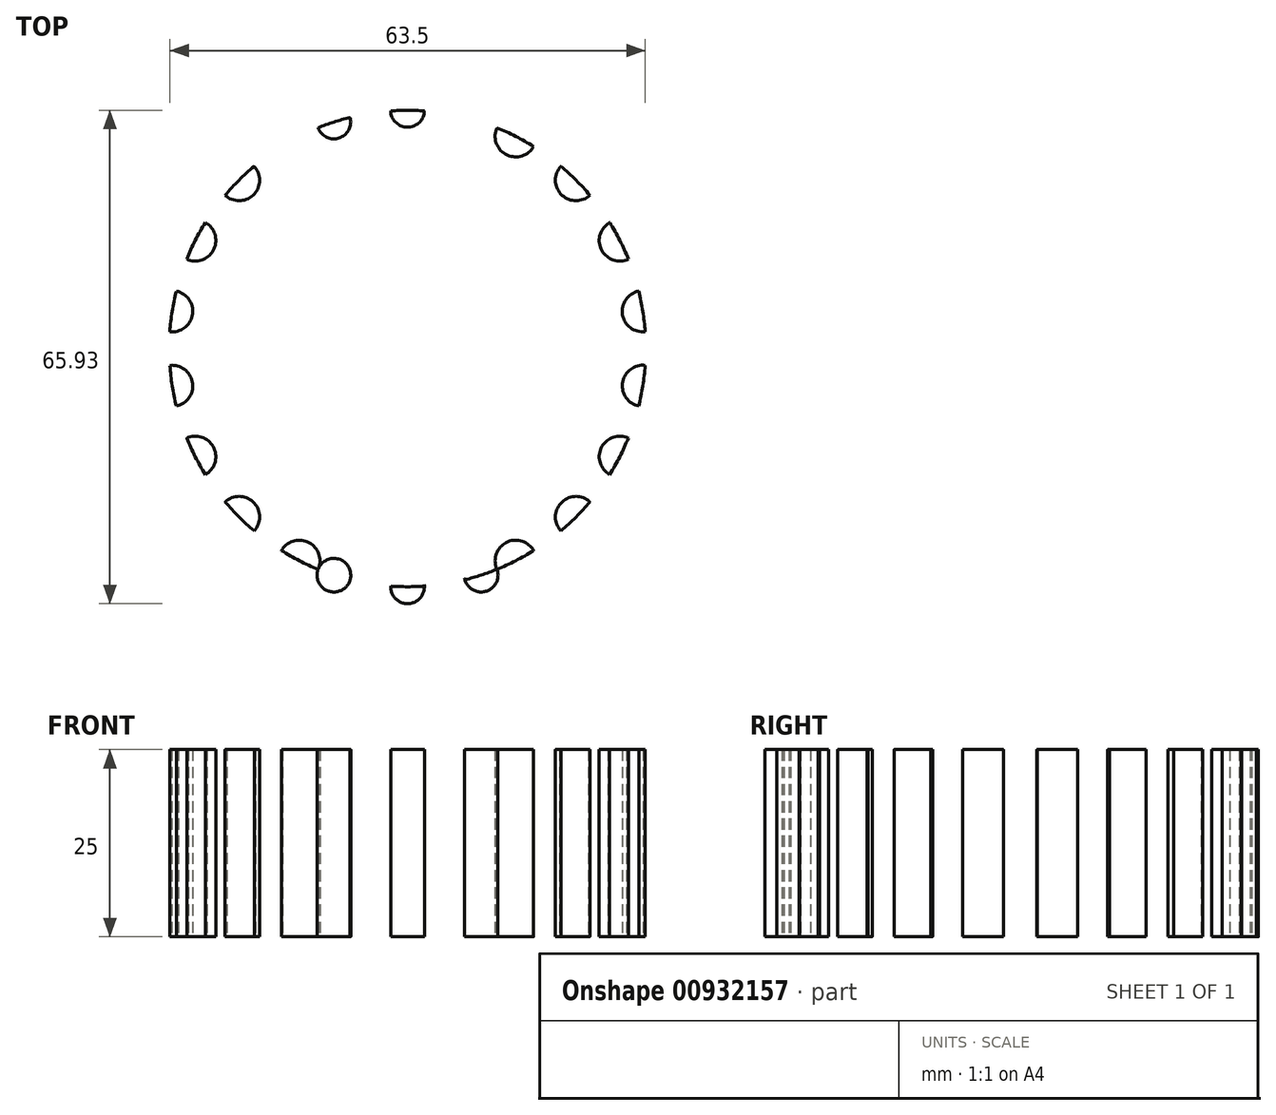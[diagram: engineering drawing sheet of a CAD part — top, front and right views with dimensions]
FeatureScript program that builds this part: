
annotation { "Feature Type Name" : "Feature", "Feature Type Description" : "" }
export const myFeature = defineFeature(function(context is Context, id is Id, definition is map)
    precondition{}
    {
        {
            var Q0;
            Q0=qCreatedBy(makeId("Top.planeOp"),FACE);
            var sketch = newSketch(context, id + "F0", { "sketchPlane" : qUnion([Q0])});
            skCircle(sketch, "E0", {"center": v(0, 0) * mm, "radius": 31.83 * mm});
            skCircle(sketch, "E1", {"center": v(0, 31.83) * mm, "radius": 2.25 * mm});
            skCircle(sketch, "E2.1.0", {"center": v(-9.84, 30.27) * mm, "radius": 2.25 * mm});
            skCircle(sketch, "E2.2.0", {"center": v(-18.71, 25.75) * mm, "radius": 2.25 * mm});
            skCircle(sketch, "E2.3.0", {"center": v(-25.76, 18.7) * mm, "radius": 2.25 * mm});
            skCircle(sketch, "E2.4.0", {"center": v(-30.28, 9.83) * mm, "radius": 2.25 * mm});
            skCircle(sketch, "E2.5.0", {"center": v(-31.84, 0) * mm, "radius": 2.25 * mm});
            skCircle(sketch, "E2.6.0", {"center": v(-30.28, -9.85) * mm, "radius": 2.25 * mm});
            skCircle(sketch, "E2.7.0", {"center": v(-25.76, -18.72) * mm, "radius": 2.25 * mm});
            skCircle(sketch, "E2.8.0", {"center": v(-18.71, -25.77) * mm, "radius": 2.25 * mm});
            skCircle(sketch, "E2.9.0", {"center": v(-9.84, -30.29) * mm, "radius": 2.25 * mm});
            skCircle(sketch, "E2.10.0", {"center": v(0, -31.85) * mm, "radius": 2.25 * mm});
            skCircle(sketch, "E2.11.0", {"center": v(9.84, -30.29) * mm, "radius": 2.25 * mm});
            skCircle(sketch, "E2.12.0", {"center": v(18.72, -25.77) * mm, "radius": 2.25 * mm});
            skCircle(sketch, "E2.13.0", {"center": v(25.76, -18.72) * mm, "radius": 2.25 * mm});
            skCircle(sketch, "E2.14.0", {"center": v(30.28, -9.85) * mm, "radius": 2.25 * mm});
            skCircle(sketch, "E2.15.0", {"center": v(31.84, 0) * mm, "radius": 2.25 * mm});
            skCircle(sketch, "E2.16.0", {"center": v(30.28, 9.83) * mm, "radius": 2.25 * mm});
            skCircle(sketch, "E2.17.0", {"center": v(25.76, 18.7) * mm, "radius": 2.25 * mm});
            skCircle(sketch, "E2.18.0", {"center": v(18.71, 25.75) * mm, "radius": 2.25 * mm});
            skCircle(sketch, "E2.19.0", {"center": v(9.84, 30.27) * mm, "radius": 2.25 * mm});
            skArc(sketch, "E3", {"start": v(-2.25, 31.75) * mm, "mid": v(-4.55, 28.72) * mm, "end": v(-7.68, 30.9) * mm});
            skArc(sketch, "E4.1.0", {"start": v(-11.95, 29.5) * mm, "mid": v(-13.2, 25.91) * mm, "end": v(-16.85, 27) * mm});
            skArc(sketch, "E4.2.0", {"start": v(-20.48, 24.37) * mm, "mid": v(-20.56, 20.56) * mm, "end": v(-24.37, 20.48) * mm});
            skArc(sketch, "E4.3.0", {"start": v(-27, 16.84) * mm, "mid": v(-25.91, 13.2) * mm, "end": v(-29.5, 11.95) * mm});
            skArc(sketch, "E4.4.0", {"start": v(-30.9, 7.67) * mm, "mid": v(-28.72, 4.55) * mm, "end": v(-31.75, 2.25) * mm});
            skArc(sketch, "E4.5.0", {"start": v(-31.75, -2.25) * mm, "mid": v(-28.72, -4.55) * mm, "end": v(-30.9, -7.68) * mm});
            skArc(sketch, "E4.6.0", {"start": v(-29.5, -11.95) * mm, "mid": v(-25.91, -13.2) * mm, "end": v(-27, -16.85) * mm});
            skArc(sketch, "E4.7.0", {"start": v(-24.37, -20.48) * mm, "mid": v(-20.56, -20.56) * mm, "end": v(-20.48, -24.37) * mm});
            skArc(sketch, "E4.8.0", {"start": v(-16.84, -27) * mm, "mid": v(-13.2, -25.91) * mm, "end": v(-11.95, -29.5) * mm});
            skArc(sketch, "E4.9.0", {"start": v(-7.67, -30.9) * mm, "mid": v(-4.55, -28.72) * mm, "end": v(-2.25, -31.75) * mm});
            skArc(sketch, "E4.10.0", {"start": v(2.25, -31.75) * mm, "mid": v(4.55, -28.72) * mm, "end": v(7.68, -30.9) * mm});
            skArc(sketch, "E4.11.0", {"start": v(11.95, -29.5) * mm, "mid": v(13.2, -25.91) * mm, "end": v(16.85, -27) * mm});
            skArc(sketch, "E4.12.0", {"start": v(20.48, -24.37) * mm, "mid": v(20.56, -20.56) * mm, "end": v(24.37, -20.48) * mm});
            skArc(sketch, "E4.13.0", {"start": v(27, -16.84) * mm, "mid": v(25.91, -13.2) * mm, "end": v(29.5, -11.95) * mm});
            skArc(sketch, "E4.14.0", {"start": v(30.9, -7.67) * mm, "mid": v(28.72, -4.55) * mm, "end": v(31.75, -2.25) * mm});
            skArc(sketch, "E4.15.0", {"start": v(31.75, 2.25) * mm, "mid": v(28.72, 4.55) * mm, "end": v(30.9, 7.68) * mm});
            skArc(sketch, "E4.16.0", {"start": v(29.5, 11.95) * mm, "mid": v(25.91, 13.2) * mm, "end": v(27, 16.85) * mm});
            skArc(sketch, "E4.17.0", {"start": v(24.37, 20.48) * mm, "mid": v(20.56, 20.56) * mm, "end": v(20.48, 24.37) * mm});
            skArc(sketch, "E4.18.0", {"start": v(16.84, 27) * mm, "mid": v(13.2, 25.91) * mm, "end": v(11.95, 29.5) * mm});
            skArc(sketch, "E4.19.0", {"start": v(7.67, 30.9) * mm, "mid": v(4.55, 28.72) * mm, "end": v(2.25, 31.75) * mm});
            skSolve(sketch);
        }
        {
            var Q0;
            {var subQ1=sQuery(id+"F0.wireOp",EDGE,"E0");var subQ20=sQuery(id+"F0.wireOp",EDGE,"E4.15.0");var subQ76=makeQuery(id+"F0.imprint","INTERSECT",VERTEX,{"disambiguationData":[OD(0.0)],"derivedFrom":[subQ1,subQ20]});Q0=makeQuery(id+"F0.imprint","IMPRINT",FACE,{"disambiguationData":[TD([[makeQuery(id+"F0.imprint","IMPRINT",EDGE,{"disambiguationData":[TD([[subQ76,1.0]])],"derivedFrom":subQ1}),1.0]])]});}
            var Q1;
            {var subQ0=sQuery(id+"F0.wireOp",EDGE,"E0");var subQ1=makeQuery(id+"F0.imprint","INTERSECT",VERTEX,{"disambiguationData":[OD(0.0)],"derivedFrom":[subQ0,sQuery(id+"F0.wireOp",EDGE,"E4.2.0")]});Q1=makeQuery(id+"F0.imprint","IMPRINT",FACE,{"disambiguationData":[TD([[makeQuery(id+"F0.imprint","IMPRINT",EDGE,{"disambiguationData":[TD([[subQ1,1.0]])],"derivedFrom":subQ0}),-1.0]])]});}
            var Q2;
            {var subQ4=sQuery(id+"F0.wireOp",EDGE,"E0");var subQ6=sQuery(id+"F0.wireOp",EDGE,"E4.2.0");var subQ8=makeQuery(id+"F0.imprint","INTERSECT",VERTEX,{"disambiguationData":[OD(0.0)],"derivedFrom":[subQ4,subQ6]});Q2=makeQuery(id+"F0.imprint","IMPRINT",FACE,{"disambiguationData":[TD([[makeQuery(id+"F0.imprint","IMPRINT",EDGE,{"disambiguationData":[TD([[subQ8,1.0]])],"derivedFrom":subQ4}),1.0]])]});}
            var Q3;
            {var subQ1=sQuery(id+"F0.wireOp",EDGE,"E0");var subQ3=makeQuery(id+"F0.imprint","INTERSECT",VERTEX,{"disambiguationData":[OD(0.0)],"derivedFrom":[subQ1,sQuery(id+"F0.wireOp",EDGE,"E4.1.0")]});Q3=makeQuery(id+"F0.imprint","IMPRINT",FACE,{"disambiguationData":[TD([[makeQuery(id+"F0.imprint","IMPRINT",EDGE,{"disambiguationData":[TD([[subQ3,-1.0]])],"derivedFrom":subQ1}),-1.0]])]});}
            var Q4;
            {var subQ1=sQuery(id+"F0.wireOp",EDGE,"E2.1.0");var subQ4=sQuery(id+"F0.wireOp",EDGE,"E4.1.0");var subQ7=makeQuery(id+"F0.imprint","INTERSECT",VERTEX,{"derivedFrom":[subQ1,subQ4]});Q4=makeQuery(id+"F0.imprint","IMPRINT",FACE,{"disambiguationData":[TD([[makeQuery(id+"F0.imprint","IMPRINT",EDGE,{"disambiguationData":[TD([[subQ7,-1.0]])],"derivedFrom":subQ1}),1.0]])]});}
            var Q5;
            {var subQ0=sQuery(id+"F0.wireOp",EDGE,"E0");var subQ1=makeQuery(id+"F0.imprint","INTERSECT",VERTEX,{"disambiguationData":[OD(1.0)],"derivedFrom":[subQ0,sQuery(id+"F0.wireOp",EDGE,"E4.19.0")]});Q5=makeQuery(id+"F0.imprint","IMPRINT",FACE,{"disambiguationData":[TD([[makeQuery(id+"F0.imprint","IMPRINT",EDGE,{"disambiguationData":[TD([[subQ1,1.0]])],"derivedFrom":subQ0}),-1.0]])]});}
            var Q6;
            {var subQ0=sQuery(id+"F0.wireOp",EDGE,"E3");var subQ1=sQuery(id+"F0.wireOp",EDGE,"E1");var subQ6=makeQuery(id+"F0.imprint","INTERSECT",VERTEX,{"derivedFrom":[subQ1,subQ0]});Q6=makeQuery(id+"F0.imprint","IMPRINT",FACE,{"disambiguationData":[TD([[makeQuery(id+"F0.imprint","IMPRINT",EDGE,{"disambiguationData":[TD([[subQ6,-1.0]])],"derivedFrom":subQ1}),1.0]])]});}
            var Q7;
            {var subQ0=sQuery(id+"F0.wireOp",EDGE,"E0");var subQ1=makeQuery(id+"F0.imprint","INTERSECT",VERTEX,{"disambiguationData":[OD(1.0)],"derivedFrom":[subQ0,sQuery(id+"F0.wireOp",EDGE,"E4.18.0")]});Q7=makeQuery(id+"F0.imprint","IMPRINT",FACE,{"disambiguationData":[TD([[makeQuery(id+"F0.imprint","IMPRINT",EDGE,{"disambiguationData":[TD([[subQ1,1.0]])],"derivedFrom":subQ0}),-1.0]])]});}
            var Q8;
            {var subQ3=sQuery(id+"F0.wireOp",EDGE,"E4.18.0");var subQ5=sQuery(id+"F0.wireOp",EDGE,"E0");var subQ8=makeQuery(id+"F0.imprint","INTERSECT",VERTEX,{"disambiguationData":[OD(1.0)],"derivedFrom":[subQ5,subQ3]});Q8=makeQuery(id+"F0.imprint","IMPRINT",FACE,{"disambiguationData":[TD([[makeQuery(id+"F0.imprint","IMPRINT",EDGE,{"disambiguationData":[TD([[subQ8,-1.0]])],"derivedFrom":subQ5}),1.0]])]});}
            var Q9;
            {var subQ0=sQuery(id+"F0.wireOp",EDGE,"E0");var subQ1=makeQuery(id+"F0.imprint","INTERSECT",VERTEX,{"disambiguationData":[OD(1.0)],"derivedFrom":[subQ0,sQuery(id+"F0.wireOp",EDGE,"E4.17.0")]});Q9=makeQuery(id+"F0.imprint","IMPRINT",FACE,{"disambiguationData":[TD([[makeQuery(id+"F0.imprint","IMPRINT",EDGE,{"disambiguationData":[TD([[subQ1,1.0]])],"derivedFrom":subQ0}),-1.0]])]});}
            var Q10;
            {var subQ0=sQuery(id+"F0.wireOp",EDGE,"E4.17.0");var subQ1=sQuery(id+"F0.wireOp",EDGE,"E0");var subQ2=makeQuery(id+"F0.imprint","INTERSECT",VERTEX,{"disambiguationData":[OD(1.0)],"derivedFrom":[subQ1,subQ0]});Q10=makeQuery(id+"F0.imprint","IMPRINT",FACE,{"disambiguationData":[TD([[makeQuery(id+"F0.imprint","IMPRINT",EDGE,{"disambiguationData":[TD([[subQ2,-1.0]])],"derivedFrom":subQ1}),1.0]])]});}
            var Q11;
            {var subQ0=sQuery(id+"F0.wireOp",EDGE,"E4.16.0");var subQ1=sQuery(id+"F0.wireOp",EDGE,"E0");var subQ2=makeQuery(id+"F0.imprint","INTERSECT",VERTEX,{"disambiguationData":[OD(1.0)],"derivedFrom":[subQ1,subQ0]});Q11=makeQuery(id+"F0.imprint","IMPRINT",FACE,{"disambiguationData":[TD([[makeQuery(id+"F0.imprint","IMPRINT",EDGE,{"disambiguationData":[TD([[subQ2,-1.0]])],"derivedFrom":subQ1}),1.0]])]});}
            var Q12;
            {var subQ0=sQuery(id+"F0.wireOp",EDGE,"E0");var subQ1=makeQuery(id+"F0.imprint","INTERSECT",VERTEX,{"disambiguationData":[OD(1.0)],"derivedFrom":[subQ0,sQuery(id+"F0.wireOp",EDGE,"E4.16.0")]});Q12=makeQuery(id+"F0.imprint","IMPRINT",FACE,{"disambiguationData":[TD([[makeQuery(id+"F0.imprint","IMPRINT",EDGE,{"disambiguationData":[TD([[subQ1,1.0]])],"derivedFrom":subQ0}),-1.0]])]});}
            var Q13;
            {var subQ0=sQuery(id+"F0.wireOp",EDGE,"E4.15.0");var subQ1=sQuery(id+"F0.wireOp",EDGE,"E0");var subQ2=makeQuery(id+"F0.imprint","INTERSECT",VERTEX,{"disambiguationData":[OD(1.0)],"derivedFrom":[subQ1,subQ0]});Q13=makeQuery(id+"F0.imprint","IMPRINT",FACE,{"disambiguationData":[TD([[makeQuery(id+"F0.imprint","IMPRINT",EDGE,{"disambiguationData":[TD([[subQ2,-1.0]])],"derivedFrom":subQ1}),1.0]])]});}
            var Q14;
            {var subQ0=sQuery(id+"F0.wireOp",EDGE,"E4.14.0");var subQ1=sQuery(id+"F0.wireOp",EDGE,"E0");var subQ2=makeQuery(id+"F0.imprint","INTERSECT",VERTEX,{"disambiguationData":[OD(1.0)],"derivedFrom":[subQ1,subQ0]});Q14=makeQuery(id+"F0.imprint","IMPRINT",FACE,{"disambiguationData":[TD([[makeQuery(id+"F0.imprint","IMPRINT",EDGE,{"disambiguationData":[TD([[subQ2,-1.0]])],"derivedFrom":subQ1}),1.0]])]});}
            var Q15;
            {var subQ0=sQuery(id+"F0.wireOp",EDGE,"E0");var subQ1=makeQuery(id+"F0.imprint","INTERSECT",VERTEX,{"disambiguationData":[OD(1.0)],"derivedFrom":[subQ0,sQuery(id+"F0.wireOp",EDGE,"E4.14.0")]});Q15=makeQuery(id+"F0.imprint","IMPRINT",FACE,{"disambiguationData":[TD([[makeQuery(id+"F0.imprint","IMPRINT",EDGE,{"disambiguationData":[TD([[subQ1,1.0]])],"derivedFrom":subQ0}),-1.0]])]});}
            var Q16;
            {var subQ0=sQuery(id+"F0.wireOp",EDGE,"E4.13.0");var subQ1=sQuery(id+"F0.wireOp",EDGE,"E0");var subQ2=makeQuery(id+"F0.imprint","INTERSECT",VERTEX,{"disambiguationData":[OD(1.0)],"derivedFrom":[subQ1,subQ0]});Q16=makeQuery(id+"F0.imprint","IMPRINT",FACE,{"disambiguationData":[TD([[makeQuery(id+"F0.imprint","IMPRINT",EDGE,{"disambiguationData":[TD([[subQ2,-1.0]])],"derivedFrom":subQ1}),1.0]])]});}
            var Q17;
            {var subQ0=sQuery(id+"F0.wireOp",EDGE,"E4.12.0");var subQ1=sQuery(id+"F0.wireOp",EDGE,"E0");var subQ2=makeQuery(id+"F0.imprint","INTERSECT",VERTEX,{"disambiguationData":[OD(1.0)],"derivedFrom":[subQ1,subQ0]});Q17=makeQuery(id+"F0.imprint","IMPRINT",FACE,{"disambiguationData":[TD([[makeQuery(id+"F0.imprint","IMPRINT",EDGE,{"disambiguationData":[TD([[subQ2,-1.0]])],"derivedFrom":subQ1}),1.0]])]});}
            var Q18;
            {var subQ0=sQuery(id+"F0.wireOp",EDGE,"E0");var subQ1=makeQuery(id+"F0.imprint","INTERSECT",VERTEX,{"disambiguationData":[OD(1.0)],"derivedFrom":[subQ0,sQuery(id+"F0.wireOp",EDGE,"E4.12.0")]});Q18=makeQuery(id+"F0.imprint","IMPRINT",FACE,{"disambiguationData":[TD([[makeQuery(id+"F0.imprint","IMPRINT",EDGE,{"disambiguationData":[TD([[subQ1,1.0]])],"derivedFrom":subQ0}),-1.0]])]});}
            var Q19;
            {var subQ0=sQuery(id+"F0.wireOp",EDGE,"E0");var subQ1=makeQuery(id+"F0.imprint","INTERSECT",VERTEX,{"disambiguationData":[OD(1.0)],"derivedFrom":[subQ0,sQuery(id+"F0.wireOp",EDGE,"E4.13.0")]});Q19=makeQuery(id+"F0.imprint","IMPRINT",FACE,{"disambiguationData":[TD([[makeQuery(id+"F0.imprint","IMPRINT",EDGE,{"disambiguationData":[TD([[subQ1,1.0]])],"derivedFrom":subQ0}),-1.0]])]});}
            var Q20;
            {var subQ0=sQuery(id+"F0.wireOp",EDGE,"E0");var subQ1=makeQuery(id+"F0.imprint","INTERSECT",VERTEX,{"disambiguationData":[OD(1.0)],"derivedFrom":[subQ0,sQuery(id+"F0.wireOp",EDGE,"E4.15.0")]});Q20=makeQuery(id+"F0.imprint","IMPRINT",FACE,{"disambiguationData":[TD([[makeQuery(id+"F0.imprint","IMPRINT",EDGE,{"disambiguationData":[TD([[subQ1,1.0]])],"derivedFrom":subQ0}),-1.0]])]});}
            var Q21;
            {var subQ0=sQuery(id+"F0.wireOp",EDGE,"E4.11.0");var subQ1=sQuery(id+"F0.wireOp",EDGE,"E0");var subQ2=makeQuery(id+"F0.imprint","INTERSECT",VERTEX,{"disambiguationData":[OD(1.0)],"derivedFrom":[subQ1,subQ0]});Q21=makeQuery(id+"F0.imprint","IMPRINT",FACE,{"disambiguationData":[TD([[makeQuery(id+"F0.imprint","IMPRINT",EDGE,{"disambiguationData":[TD([[subQ2,-1.0]])],"derivedFrom":subQ1}),1.0]])]});}
            var Q22;
            {var subQ0=sQuery(id+"F0.wireOp",EDGE,"E0");var subQ1=makeQuery(id+"F0.imprint","INTERSECT",VERTEX,{"disambiguationData":[OD(1.0)],"derivedFrom":[subQ0,sQuery(id+"F0.wireOp",EDGE,"E4.11.0")]});Q22=makeQuery(id+"F0.imprint","IMPRINT",FACE,{"disambiguationData":[TD([[makeQuery(id+"F0.imprint","IMPRINT",EDGE,{"disambiguationData":[TD([[subQ1,1.0]])],"derivedFrom":subQ0}),-1.0]])]});}
            var Q23;
            {var subQ0=sQuery(id+"F0.wireOp",EDGE,"E0");var subQ1=makeQuery(id+"F0.imprint","INTERSECT",VERTEX,{"disambiguationData":[OD(1.0)],"derivedFrom":[subQ0,sQuery(id+"F0.wireOp",EDGE,"E4.10.0")]});Q23=makeQuery(id+"F0.imprint","IMPRINT",FACE,{"disambiguationData":[TD([[makeQuery(id+"F0.imprint","IMPRINT",EDGE,{"disambiguationData":[TD([[subQ1,1.0]])],"derivedFrom":subQ0}),-1.0]])]});}
            var Q24;
            {var subQ4=sQuery(id+"F0.wireOp",EDGE,"E4.10.0");var subQ6=sQuery(id+"F0.wireOp",EDGE,"E0");var subQ8=makeQuery(id+"F0.imprint","INTERSECT",VERTEX,{"disambiguationData":[OD(0.0)],"derivedFrom":[subQ6,subQ4]});Q24=makeQuery(id+"F0.imprint","IMPRINT",FACE,{"disambiguationData":[TD([[makeQuery(id+"F0.imprint","IMPRINT",EDGE,{"disambiguationData":[TD([[subQ8,1.0]])],"derivedFrom":subQ6}),1.0]])]});}
            var Q25;
            {var subQ0=sQuery(id+"F0.wireOp",EDGE,"E0");var subQ1=makeQuery(id+"F0.imprint","INTERSECT",VERTEX,{"disambiguationData":[OD(0.0)],"derivedFrom":[subQ0,sQuery(id+"F0.wireOp",EDGE,"E4.10.0")]});Q25=makeQuery(id+"F0.imprint","IMPRINT",FACE,{"disambiguationData":[TD([[makeQuery(id+"F0.imprint","IMPRINT",EDGE,{"disambiguationData":[TD([[subQ1,1.0]])],"derivedFrom":subQ0}),-1.0]])]});}
            var Q26;
            {var subQ0=sQuery(id+"F0.wireOp",EDGE,"E0");var subQ1=makeQuery(id+"F0.imprint","INTERSECT",VERTEX,{"derivedFrom":[subQ0,sQuery(id+"F0.wireOp",EDGE,"E4.9.0")]});Q26=makeQuery(id+"F0.imprint","IMPRINT",FACE,{"disambiguationData":[TD([[makeQuery(id+"F0.imprint","IMPRINT",EDGE,{"disambiguationData":[TD([[subQ1,1.0]])],"derivedFrom":subQ0}),-1.0]])]});}
            var Q27;
            {var subQ0=sQuery(id+"F0.wireOp",EDGE,"E0");var subQ1=makeQuery(id+"F0.imprint","INTERSECT",VERTEX,{"disambiguationData":[OD(0.0)],"derivedFrom":[subQ0,sQuery(id+"F0.wireOp",EDGE,"E4.8.0")]});Q27=makeQuery(id+"F0.imprint","IMPRINT",FACE,{"disambiguationData":[TD([[makeQuery(id+"F0.imprint","IMPRINT",EDGE,{"disambiguationData":[TD([[subQ1,1.0]])],"derivedFrom":subQ0}),-1.0]])]});}
            var Q28;
            {var subQ0=sQuery(id+"F0.wireOp",EDGE,"E0");var subQ1=makeQuery(id+"F0.imprint","INTERSECT",VERTEX,{"disambiguationData":[OD(0.0)],"derivedFrom":[subQ0,sQuery(id+"F0.wireOp",EDGE,"E4.7.0")]});Q28=makeQuery(id+"F0.imprint","IMPRINT",FACE,{"disambiguationData":[TD([[makeQuery(id+"F0.imprint","IMPRINT",EDGE,{"disambiguationData":[TD([[subQ1,1.0]])],"derivedFrom":subQ0}),-1.0]])]});}
            var Q29;
            {var subQ0=sQuery(id+"F0.wireOp",EDGE,"E4.7.0");var subQ1=sQuery(id+"F0.wireOp",EDGE,"E0");var subQ2=makeQuery(id+"F0.imprint","INTERSECT",VERTEX,{"disambiguationData":[OD(0.0)],"derivedFrom":[subQ1,subQ0]});Q29=makeQuery(id+"F0.imprint","IMPRINT",FACE,{"disambiguationData":[TD([[makeQuery(id+"F0.imprint","IMPRINT",EDGE,{"disambiguationData":[TD([[subQ2,1.0]])],"derivedFrom":subQ1}),1.0]])]});}
            var Q30;
            {var subQ0=sQuery(id+"F0.wireOp",EDGE,"E4.8.0");var subQ1=sQuery(id+"F0.wireOp",EDGE,"E0");var subQ2=makeQuery(id+"F0.imprint","INTERSECT",VERTEX,{"disambiguationData":[OD(0.0)],"derivedFrom":[subQ1,subQ0]});Q30=makeQuery(id+"F0.imprint","IMPRINT",FACE,{"disambiguationData":[TD([[makeQuery(id+"F0.imprint","IMPRINT",EDGE,{"disambiguationData":[TD([[subQ2,1.0]])],"derivedFrom":subQ1}),1.0]])]});}
            var Q31;
            {var subQ4=sQuery(id+"F0.wireOp",EDGE,"E0");var subQ6=sQuery(id+"F0.wireOp",EDGE,"E4.9.0");var subQ8=makeQuery(id+"F0.imprint","INTERSECT",VERTEX,{"derivedFrom":[subQ4,subQ6]});Q31=makeQuery(id+"F0.imprint","IMPRINT",FACE,{"disambiguationData":[TD([[makeQuery(id+"F0.imprint","IMPRINT",EDGE,{"disambiguationData":[TD([[subQ8,1.0]])],"derivedFrom":subQ4}),1.0]])]});}
            var Q32;
            {var subQ0=sQuery(id+"F0.wireOp",EDGE,"E4.10.0");var subQ1=sQuery(id+"F0.wireOp",EDGE,"E0");var subQ2=makeQuery(id+"F0.imprint","INTERSECT",VERTEX,{"disambiguationData":[OD(1.0)],"derivedFrom":[subQ1,subQ0]});Q32=makeQuery(id+"F0.imprint","IMPRINT",FACE,{"disambiguationData":[TD([[makeQuery(id+"F0.imprint","IMPRINT",EDGE,{"disambiguationData":[TD([[subQ2,-1.0]])],"derivedFrom":subQ1}),1.0]])]});}
            var Q33;
            {var subQ0=sQuery(id+"F0.wireOp",EDGE,"E0");var subQ1=makeQuery(id+"F0.imprint","INTERSECT",VERTEX,{"disambiguationData":[OD(0.0)],"derivedFrom":[subQ0,sQuery(id+"F0.wireOp",EDGE,"E4.6.0")]});Q33=makeQuery(id+"F0.imprint","IMPRINT",FACE,{"disambiguationData":[TD([[makeQuery(id+"F0.imprint","IMPRINT",EDGE,{"disambiguationData":[TD([[subQ1,1.0]])],"derivedFrom":subQ0}),-1.0]])]});}
            var Q34;
            {var subQ0=sQuery(id+"F0.wireOp",EDGE,"E4.6.0");var subQ1=sQuery(id+"F0.wireOp",EDGE,"E0");var subQ2=makeQuery(id+"F0.imprint","INTERSECT",VERTEX,{"disambiguationData":[OD(0.0)],"derivedFrom":[subQ1,subQ0]});Q34=makeQuery(id+"F0.imprint","IMPRINT",FACE,{"disambiguationData":[TD([[makeQuery(id+"F0.imprint","IMPRINT",EDGE,{"disambiguationData":[TD([[subQ2,1.0]])],"derivedFrom":subQ1}),1.0]])]});}
            var Q35;
            {var subQ0=sQuery(id+"F0.wireOp",EDGE,"E4.5.0");var subQ1=sQuery(id+"F0.wireOp",EDGE,"E0");var subQ2=makeQuery(id+"F0.imprint","INTERSECT",VERTEX,{"disambiguationData":[OD(0.0)],"derivedFrom":[subQ1,subQ0]});Q35=makeQuery(id+"F0.imprint","IMPRINT",FACE,{"disambiguationData":[TD([[makeQuery(id+"F0.imprint","IMPRINT",EDGE,{"disambiguationData":[TD([[subQ2,1.0]])],"derivedFrom":subQ1}),1.0]])]});}
            var Q36;
            {var subQ0=sQuery(id+"F0.wireOp",EDGE,"E0");var subQ1=makeQuery(id+"F0.imprint","INTERSECT",VERTEX,{"disambiguationData":[OD(0.0)],"derivedFrom":[subQ0,sQuery(id+"F0.wireOp",EDGE,"E4.5.0")]});Q36=makeQuery(id+"F0.imprint","IMPRINT",FACE,{"disambiguationData":[TD([[makeQuery(id+"F0.imprint","IMPRINT",EDGE,{"disambiguationData":[TD([[subQ1,1.0]])],"derivedFrom":subQ0}),-1.0]])]});}
            var Q37;
            {var subQ0=sQuery(id+"F0.wireOp",EDGE,"E0");var subQ1=makeQuery(id+"F0.imprint","INTERSECT",VERTEX,{"disambiguationData":[OD(0.0)],"derivedFrom":[subQ0,sQuery(id+"F0.wireOp",EDGE,"E4.4.0")]});Q37=makeQuery(id+"F0.imprint","IMPRINT",FACE,{"disambiguationData":[TD([[makeQuery(id+"F0.imprint","IMPRINT",EDGE,{"disambiguationData":[TD([[subQ1,1.0]])],"derivedFrom":subQ0}),-1.0]])]});}
            var Q38;
            {var subQ0=sQuery(id+"F0.wireOp",EDGE,"E4.4.0");var subQ1=sQuery(id+"F0.wireOp",EDGE,"E0");var subQ2=makeQuery(id+"F0.imprint","INTERSECT",VERTEX,{"disambiguationData":[OD(0.0)],"derivedFrom":[subQ1,subQ0]});Q38=makeQuery(id+"F0.imprint","IMPRINT",FACE,{"disambiguationData":[TD([[makeQuery(id+"F0.imprint","IMPRINT",EDGE,{"disambiguationData":[TD([[subQ2,1.0]])],"derivedFrom":subQ1}),1.0]])]});}
            var Q39;
            {var subQ0=sQuery(id+"F0.wireOp",EDGE,"E4.3.0");var subQ1=sQuery(id+"F0.wireOp",EDGE,"E0");var subQ2=makeQuery(id+"F0.imprint","INTERSECT",VERTEX,{"disambiguationData":[OD(0.0)],"derivedFrom":[subQ1,subQ0]});Q39=makeQuery(id+"F0.imprint","IMPRINT",FACE,{"disambiguationData":[TD([[makeQuery(id+"F0.imprint","IMPRINT",EDGE,{"disambiguationData":[TD([[subQ2,1.0]])],"derivedFrom":subQ1}),1.0]])]});}
            var Q40;
            {var subQ0=sQuery(id+"F0.wireOp",EDGE,"E0");var subQ1=makeQuery(id+"F0.imprint","INTERSECT",VERTEX,{"disambiguationData":[OD(0.0)],"derivedFrom":[subQ0,sQuery(id+"F0.wireOp",EDGE,"E4.3.0")]});Q40=makeQuery(id+"F0.imprint","IMPRINT",FACE,{"disambiguationData":[TD([[makeQuery(id+"F0.imprint","IMPRINT",EDGE,{"disambiguationData":[TD([[subQ1,1.0]])],"derivedFrom":subQ0}),-1.0]])]});}
            extrude(context, id + "F1", {"entities" : qUnion([Q0, Q1, Q2, Q3, Q4, Q5, Q6, Q7, Q8, Q9, Q10, Q11, Q12, Q13, Q14, Q15, Q16, Q17, Q18, Q19, Q20, Q21, Q22, Q23, Q24, Q25, Q26, Q27, Q28, Q29, Q30, Q31, Q32, Q33, Q34, Q35, Q36, Q37, Q38, Q39, Q40]), "depth" : 25 * mm, "offsetDistance" : 25 * mm});
        }
        {
            var Q0;
            Q0=sQuery(id+"F0.wireOp",VERTEX,"E0.center");
            var Q1;
            Q1=makeQuery(id+"F1.opExtrude","SWEPT_BODY",BODY,{"disambiguationData":[OSD([sQuery(id+"F0.wireOp",EDGE,"E0"),sQuery(id+"F0.wireOp",EDGE,"E1"),sQuery(id+"F0.wireOp",EDGE,"E2.1.0"),sQuery(id+"F0.wireOp",EDGE,"E2.2.0"),sQuery(id+"F0.wireOp",EDGE,"E2.3.0"),sQuery(id+"F0.wireOp",EDGE,"E2.4.0"),sQuery(id+"F0.wireOp",EDGE,"E2.5.0"),sQuery(id+"F0.wireOp",EDGE,"E2.6.0"),sQuery(id+"F0.wireOp",EDGE,"E2.7.0"),sQuery(id+"F0.wireOp",EDGE,"E2.8.0"),sQuery(id+"F0.wireOp",EDGE,"E2.9.0"),sQuery(id+"F0.wireOp",EDGE,"E2.10.0"),sQuery(id+"F0.wireOp",EDGE,"E2.11.0"),sQuery(id+"F0.wireOp",EDGE,"E2.12.0"),sQuery(id+"F0.wireOp",EDGE,"E2.13.0"),sQuery(id+"F0.wireOp",EDGE,"E2.14.0"),sQuery(id+"F0.wireOp",EDGE,"E2.15.0"),sQuery(id+"F0.wireOp",EDGE,"E2.16.0"),sQuery(id+"F0.wireOp",EDGE,"E2.17.0"),sQuery(id+"F0.wireOp",EDGE,"E2.18.0"),sQuery(id+"F0.wireOp",EDGE,"E2.19.0"),sQuery(id+"F0.wireOp",EDGE,"E3"),sQuery(id+"F0.wireOp",EDGE,"E4.1.0"),sQuery(id+"F0.wireOp",EDGE,"E4.2.0"),sQuery(id+"F0.wireOp",EDGE,"E4.3.0"),sQuery(id+"F0.wireOp",EDGE,"E4.4.0"),sQuery(id+"F0.wireOp",EDGE,"E4.5.0"),sQuery(id+"F0.wireOp",EDGE,"E4.6.0"),sQuery(id+"F0.wireOp",EDGE,"E4.7.0"),sQuery(id+"F0.wireOp",EDGE,"E4.8.0"),sQuery(id+"F0.wireOp",EDGE,"E4.9.0"),sQuery(id+"F0.wireOp",EDGE,"E4.10.0"),sQuery(id+"F0.wireOp",EDGE,"E4.11.0"),sQuery(id+"F0.wireOp",EDGE,"E4.12.0"),sQuery(id+"F0.wireOp",EDGE,"E4.13.0"),sQuery(id+"F0.wireOp",EDGE,"E4.14.0"),sQuery(id+"F0.wireOp",EDGE,"E4.15.0"),sQuery(id+"F0.wireOp",EDGE,"E4.16.0"),sQuery(id+"F0.wireOp",EDGE,"E4.17.0"),sQuery(id+"F0.wireOp",EDGE,"E4.18.0"),sQuery(id+"F0.wireOp",EDGE,"E4.19.0")])]});
            hole(context, id + "F2", {"style" : HoleStyle.SIMPLE, "endStyle" : HoleEndStyle.THROUGH, "oppositeDirection" : true, "holeDiameter" : 3.5 * mm, "majorDiameter" : 5 * mm, "isTappedThrough" : true, "tappedDepth" : 12 * mm, "tapClearance" : 3, "locations" : qUnion([Q0]), "scope" : qUnion([Q1])});
        }
    });
